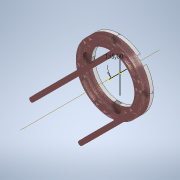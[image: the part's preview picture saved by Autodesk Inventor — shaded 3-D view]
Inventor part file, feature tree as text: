
AUTODESK INVENTOR PART (.ipt)
format: ipt  version: 2022 (Build 260153000, 153)  size: 395,776 bytes
history: native  units: mm
features: sketch x4, extrude x3, other x2, plane x1
ambient origin geometry x8: Origin, YZ Plane, XZ Plane, XY Plane, X Axis, Y Axis, Z Axis, Center Point
bodies: Solid1 (feature_tree)
feature tree (10):
  other  "holder"
  sketch  "Sketch1"  dims[d0=11.0mm d1=40.0mm d3=360.0deg]
  extrude  "Extrusion1"  Depth=40.0mm TaperAngle=360.0deg
  extrude  "Extrusion2"  Depth=3.5mm TaperAngle=0.0deg
  sketch  "Sketch3"  dims[d5=4.0mm d6=0.0mm d7=3.5mm d8=0.0mm]
  sketch  "Sketch4"  dims[d9=135.0deg d10=90.0deg]
  plane  "Work Plane1"
  extrude  "Extrusion3"  TaperAngle=90.0deg  [1 undecoded]
  sketch  "Sketch5"  dims[d11=10.0mm d12=0.0mm]
  other  "MeshFeature1"
note: 1 required parameter value undecoded (feature->parameter linkage not recoverable at this tier; creation-order binding heuristic only, values carry confidence <= 0.55)
